# Revit family: UB90.xxx.UL.T_RVT15
name_source: partatom
category: Möbelsysteme
revit_build: Autodesk Revit 2015 (Build: 20160512_1515(x64)
units: mm (PartAtom-declared; Revit-internal decimal feet)

## types (6) — shared parameters
1100/500 2T 2nd lvl = Nein
1100/600 2T 2nd lvl = Nein
590/500 2nd lvl = Nein
590/600 2nd lvl = Nein
890/500 2T 2nd lvl = Nein
890/600 2T 2nd lvl = Nein
Beschreibung = GS-tested safety storage underbench cabinets for unrestricted storage of flammable hazardous materials in work areas in accordance with EN 14470-1 and TRGS 510 with a fire resistance of 90 (Type 90)
Cabinet & door colour = RAL 7035 Light grey
Cabinet height = 600 mm
Diff. pressure (Air change 10 times) = 1.0 Pa
Hersteller = asecos GmbH
Price information = Price from fall 2017
Price information 2 = Prices are ex works and without taxes and shipping
Product video = https://www.youtube.com
URL = https://www.asecos.com
ex. air pos. 2 = 130 mm  [stored 0.426509 ft]

## per-type parameters (varying)
| type | 1100/500 2T perf. insert | 1100/600 2T perf. insert | 590/500 perf. insert | 590/600 perf. insert | 890/500 2T perf. insert | 890/600 2T perf. insert | Air change 10 times | Bestellnummer DACH | Cabinet depth | Cabinet width | Distributed load | Door width | Door width RS | Double door | Handle position | Kosten | Modell | Order No. Global | Single door | Sticker HI | Sticker LO | Typenbild | ex. air pos. 1 |
| UB90.060.089.UL.2T | Nein | Nein | Nein | Nein | Nein | Ja | 0.6 L/s | 37020-001-33767 | 574 mm  [stored 1.8832 ft] | 893 mm  [stored 2.92979 ft] | 3.07 kN/m² | 416 mm | 416 mm | Ja | 49 mm  [stored 0.160761 ft] | 1771.5 $ | UB90.060.089.UL.2T, light grey, bottom collecting sump with perforated insert | 37020-001-33767 | Nein | Nein | Ja | 30464-001.jpg (2) | 301 mm  [stored 0.987533 ft] |
| UB90.060.059.050.UL.T | Nein | Nein | Ja | Nein | Nein | Nein | 0.3 L/s | 36997-001-33765 | 503 mm | 593 mm  [stored 1.94554 ft] | 4.51 kN/m² | 539 mm | 495 mm | Nein | 73 mm | 1318 $ | UB90.060.059.050.UL.T, light grey, bottom collecting sump with perforated insert | 36997-001-33765 | Ja | Ja | Nein | 30483-001.jpg (2) | 182 mm |
| UB90.060.059.UL.T | Nein | Nein | Nein | Ja | Nein | Nein | 0.3 L/s | 37007-001-33763 | 574 mm  [stored 1.8832 ft] | 593 mm  [stored 1.94554 ft] | 4.41 kN/m² | 539 mm | 495 mm | Nein | 73 mm | 1318 $ | UB90.060.059.UL.T, light grey, bottom collecting sump with perforated insert | 37007-001-33763 | Ja | Ja | Nein | 30481-001.jpg (2) | 182 mm |
| UB90.060.110.050.UL.2T | Ja | Nein | Nein | Nein | Nein | Nein | 0.6 L/s | 37035-001-33775 | 503 mm | 1102 mm  [stored 3.61549 ft] | 2.73 kN/m² | 521 mm  [stored 1.70932 ft] | 521 mm  [stored 1.70932 ft] | Ja | 49 mm  [stored 0.160761 ft] | 1838.5 $ | UB90.060.110.050.UL.2T, light grey, bottom collecting sump with perforated insert | 37035-001-33775 | Nein | Ja | Nein | 30444-001.jpg (2) | 301 mm  [stored 0.987533 ft] |
| UB90.060.089.050.UL.2T | Nein | Nein | Nein | Nein | Ja | Nein | 0.3 L/s | 37013-001-33769 | 503 mm | 893 mm  [stored 2.92979 ft] | 3.11 kN/m² | 416 mm | 416 mm | Ja | 49 mm  [stored 0.160761 ft] | 1771.5 $ | UB90.060.089.050.UL.2T, light grey, bottom collecting sump with perforated insert | 37013-001-33769 | Nein | Nein | Ja | 30465-001.jpg (2) | 301 mm  [stored 0.987533 ft] |
| UB90.060.110.UL.2T | Nein | Ja | Nein | Nein | Nein | Nein | 0.6 L/s | 37050-001-33771 | 574 mm  [stored 1.8832 ft] | 1102 mm  [stored 3.61549 ft] | 2.72 kN/m² | 521 mm  [stored 1.70932 ft] | 521 mm  [stored 1.70932 ft] | Ja | 49 mm  [stored 0.160761 ft] | 1838.5 $ | UB90.060.110.UL.2T, light grey, bottom collecting sump with perforated insert | 37050-001-33771 | Nein | Ja | Nein | 30443-001.jpg (2) | 301 mm  [stored 0.987533 ft] |

note: [stored X ft] marks values corroborated as IEEE doubles in the binary element streams (Revit-internal decimal feet)
